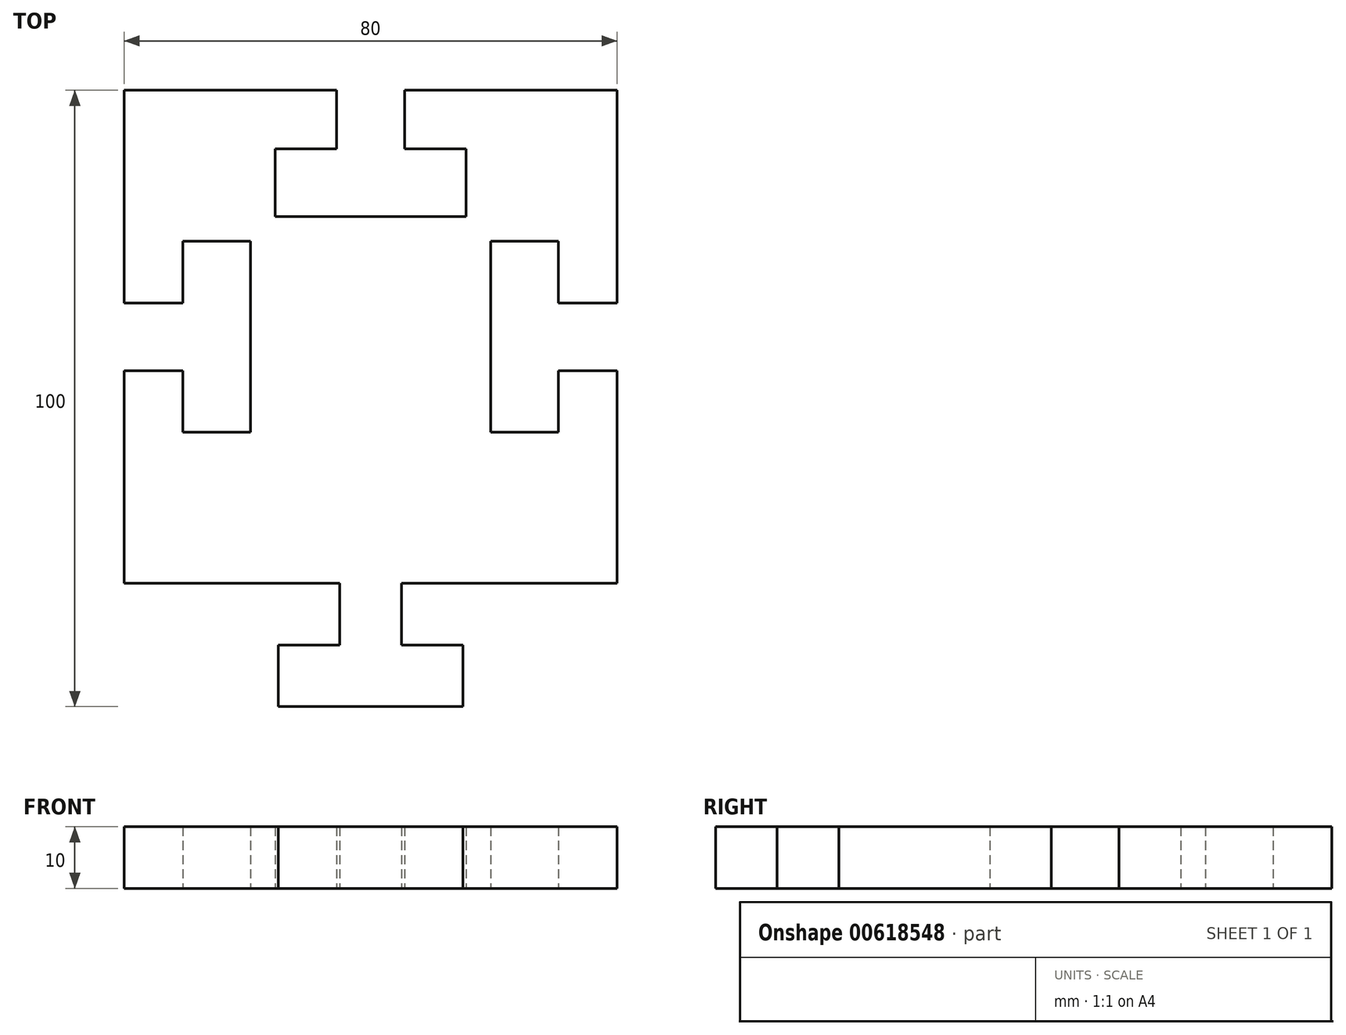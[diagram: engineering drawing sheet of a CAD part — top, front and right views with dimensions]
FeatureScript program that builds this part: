
annotation { "Feature Type Name" : "Feature", "Feature Type Description" : "" }
export const myFeature = defineFeature(function(context is Context, id is Id, definition is map)
    precondition{}
    {
        {
            var Q0;
            Q0=qCreatedBy(makeId("Top.planeOp"),FACE);
            var sketch = newSketch(context, id + "F0", { "sketchPlane" : qUnion([Q0])});
            skLineSegment(sketch, "E0.bottom", {"start": v(-40, 39.28) * mm, "end": v(-5.5, 39.28) * mm});
            skLineSegment(sketch, "E0.left", {"start": v(-40, 39.28) * mm, "end": v(-40, 4.78) * mm});
            skLineSegment(sketch, "E0.right", {"start": v(40, 39.28) * mm, "end": v(40, 4.78) * mm});
            skLineSegment(sketch, "E1", {"start": v(-5, -40.72) * mm, "end": v(-5, -50.72) * mm});
            skLineSegment(sketch, "E2", {"start": v(-5, -50.72) * mm, "end": v(-15, -50.72) * mm});
            skLineSegment(sketch, "E3", {"start": v(-15, -50.72) * mm, "end": v(-15, -60.72) * mm});
            skLineSegment(sketch, "E4", {"start": v(-15, -60.72) * mm, "end": v(15, -60.72) * mm});
            skPoint(sketch, "E5.end.orphan", {"position": v(0, -40.72) * mm});
            skLineSegment(sketch, "E6", {"start": v(15, -60.72) * mm, "end": v(15, -50.72) * mm});
            skLineSegment(sketch, "E7", {"start": v(15, -50.72) * mm, "end": v(5, -50.72) * mm});
            skLineSegment(sketch, "E8", {"start": v(5, -50.72) * mm, "end": v(5, -40.72) * mm});
            skLineSegment(sketch, "E9.trimOffspring", {"start": v(5, -40.72) * mm, "end": v(40, -40.72) * mm});
            skLineSegment(sketch, "E10", {"start": v(-5, -40.72) * mm, "end": v(-40, -40.72) * mm});
            skPoint(sketch, "E11.MirrorCS.start.orphan", {"position": v(-5, -40.72) * mm});
            skPoint(sketch, "E12.MirrorCS.end.orphan", {"position": v(5, -40.72) * mm});
            skLineSegment(sketch, "E13.1.0", {"start": v(19.5, -16.22) * mm, "end": v(19.5, 14.78) * mm});
            skLineSegment(sketch, "E13.1.1", {"start": v(30.5, -16.22) * mm, "end": v(19.5, -16.22) * mm});
            skLineSegment(sketch, "E13.1.2", {"start": v(30.5, -6.22) * mm, "end": v(30.5, -16.22) * mm});
            skLineSegment(sketch, "E13.1.3", {"start": v(40, -6.22) * mm, "end": v(30.5, -6.22) * mm});
            skLineSegment(sketch, "E13.1.4", {"start": v(30.5, 4.78) * mm, "end": v(40, 4.78) * mm});
            skLineSegment(sketch, "E13.1.5", {"start": v(30.5, 14.78) * mm, "end": v(30.5, 4.78) * mm});
            skLineSegment(sketch, "E13.1.6", {"start": v(19.5, 14.78) * mm, "end": v(30.5, 14.78) * mm});
            skLineSegment(sketch, "E13.2.0", {"start": v(15.5, 18.78) * mm, "end": v(-15.5, 18.78) * mm});
            skLineSegment(sketch, "E13.2.1", {"start": v(15.5, 29.78) * mm, "end": v(15.5, 18.78) * mm});
            skLineSegment(sketch, "E13.2.2", {"start": v(5.5, 29.78) * mm, "end": v(15.5, 29.78) * mm});
            skLineSegment(sketch, "E13.2.3", {"start": v(5.5, 39.28) * mm, "end": v(5.5, 29.78) * mm});
            skLineSegment(sketch, "E13.2.4", {"start": v(-5.5, 29.78) * mm, "end": v(-5.5, 39.28) * mm});
            skLineSegment(sketch, "E13.2.5", {"start": v(-15.5, 29.78) * mm, "end": v(-5.5, 29.78) * mm});
            skLineSegment(sketch, "E13.2.6", {"start": v(-15.5, 18.78) * mm, "end": v(-15.5, 29.78) * mm});
            skLineSegment(sketch, "E13.3.0", {"start": v(-19.5, 14.78) * mm, "end": v(-19.5, -16.22) * mm});
            skLineSegment(sketch, "E13.3.1", {"start": v(-30.5, 14.78) * mm, "end": v(-19.5, 14.78) * mm});
            skLineSegment(sketch, "E13.3.2", {"start": v(-30.5, 4.78) * mm, "end": v(-30.5, 14.78) * mm});
            skLineSegment(sketch, "E13.3.3", {"start": v(-40, 4.78) * mm, "end": v(-30.5, 4.78) * mm});
            skLineSegment(sketch, "E13.3.4", {"start": v(-30.5, -6.22) * mm, "end": v(-40, -6.22) * mm});
            skLineSegment(sketch, "E13.3.5", {"start": v(-30.5, -16.22) * mm, "end": v(-30.5, -6.22) * mm});
            skLineSegment(sketch, "E13.3.6", {"start": v(-19.5, -16.22) * mm, "end": v(-30.5, -16.22) * mm});
            skPoint(sketch, "E13.center", {"position": v(0, -0.72) * mm});
            skLineSegment(sketch, "E14.trimOffspring", {"start": v(-40, -6.22) * mm, "end": v(-40, -40.72) * mm});
            skLineSegment(sketch, "E15.trimOffspring", {"start": v(5.5, 39.28) * mm, "end": v(40, 39.28) * mm});
            skLineSegment(sketch, "E16.trimOffspring", {"start": v(40, -6.22) * mm, "end": v(40, -40.72) * mm});
            skSolve(sketch);
        }
        {
            var Q0;
            Q0=makeQuery(id+"F0.imprint","IMPRINT",FACE,{"disambiguationData":[TD([[makeQuery(id+"F0.imprint","IMPRINT",EDGE,{"derivedFrom":sQuery(id+"F0.wireOp",EDGE,"E0.bottom")}),-1.0]])]});
            extrude(context, id + "F1", {"entities" : qUnion([Q0]), "depth" : 10 * mm, "offsetDistance" : 25 * mm});
        }
    });
